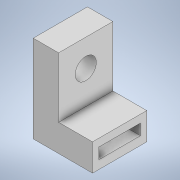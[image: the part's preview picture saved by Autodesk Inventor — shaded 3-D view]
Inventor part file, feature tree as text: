
AUTODESK INVENTOR PART (.ipt)
format: ipt  version: 2020 (Build 240168000, 168)  size: 257,536 bytes
history: native  units: mm
features: extrude x2, sketch x2
ambient origin geometry x8: Origin, YZ Plane, XZ Plane, XY Plane, X Axis, Y Axis, Z Axis, Center Point
bodies: Solid1 (feature_tree)
feature tree (4):
  extrude  "Extrusion1"  Depth=16.0mm
  extrude  "Extrusion2"  Depth=1.875mm
  sketch  "Sketch1"  dims[d0=25.75mm d1=16.0mm]
  sketch  "Sketch2"  dims[d2=2.5mm d4=1.875mm d5=1.875mm d6=3.25mm d7=6.25mm d8=7.5mm d9=0.0mm d10=8.0mm d11=10.0mm d12=0.0mm d13=0.5mm d14=0.872665mm]
